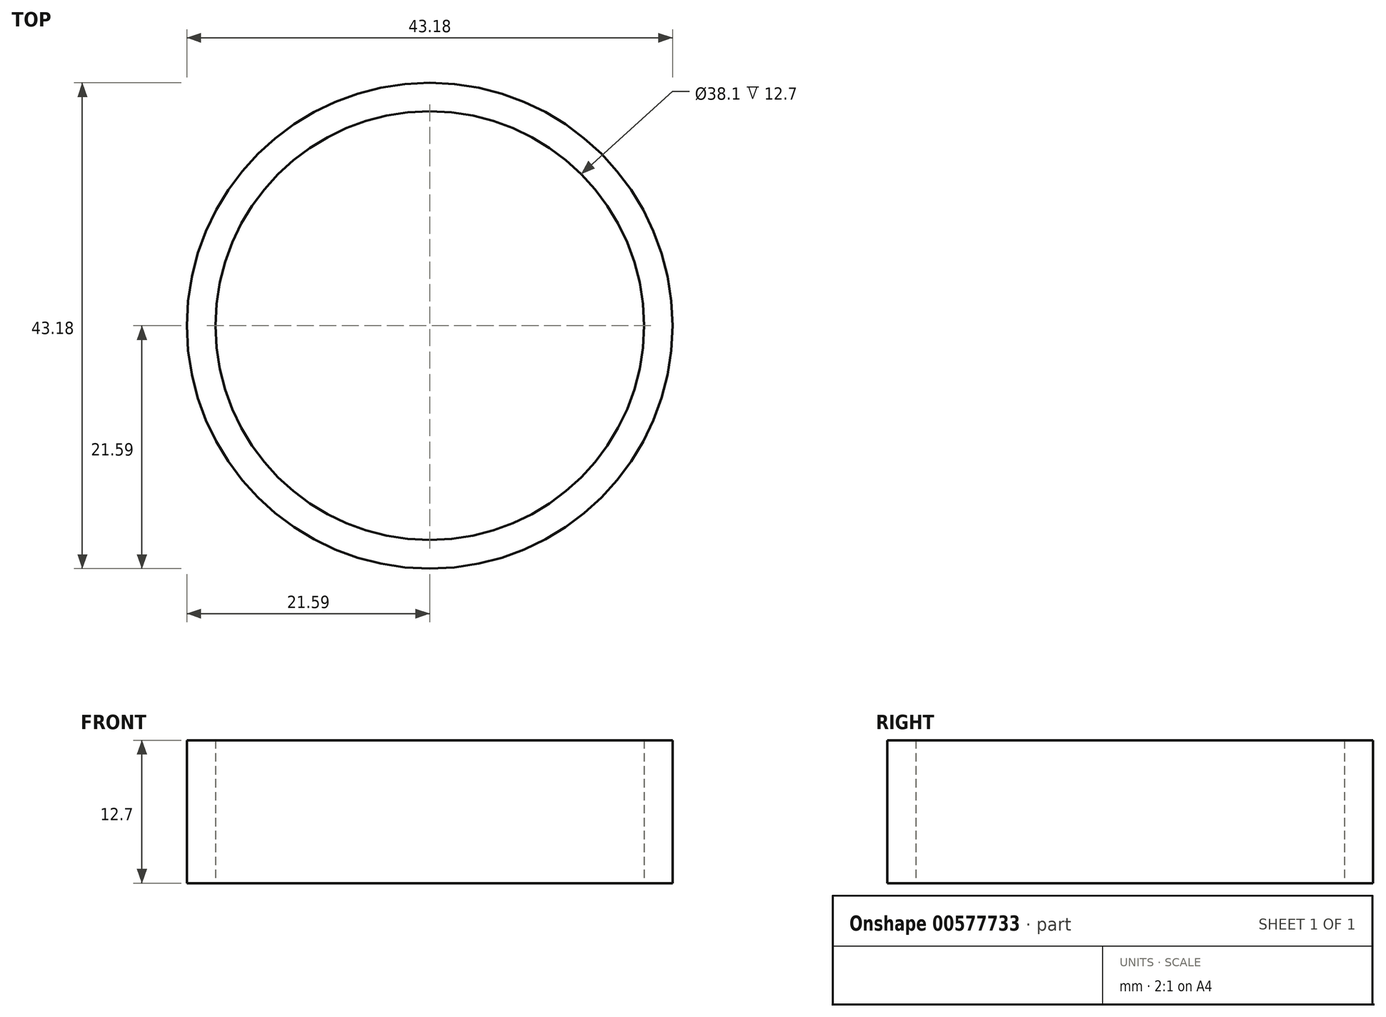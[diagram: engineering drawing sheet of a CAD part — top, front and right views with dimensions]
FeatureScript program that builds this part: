
annotation { "Feature Type Name" : "Feature", "Feature Type Description" : "" }
export const myFeature = defineFeature(function(context is Context, id is Id, definition is map)
    precondition{}
    {
        {
            var Q0;
            Q0=qCreatedBy(makeId("Top.planeOp"),FACE);
            var sketch = newSketch(context, id + "F0", { "sketchPlane" : qUnion([Q0])});
            skCircle(sketch, "E0", {"center": v(0, 0) * mm, "radius": 21.6 * mm});
            skSolve(sketch);
        }
        {
            var Q0;
            Q0=makeQuery(id+"F0.imprint","IMPRINT",FACE,{"disambiguationData":[TD([[makeQuery(id+"F0.imprint","IMPRINT",EDGE,{"derivedFrom":sQuery(id+"F0.wireOp",EDGE,"E0")}),1.0]])]});
            extrude(context, id + "F1", {"entities" : qUnion([Q0]), "depth" : 12.7 * mm, "offsetDistance" : 25.4 * mm});
        }
        {
            var Q0;
            Q0=qCreatedBy(makeId("Top.planeOp"),FACE);
            var sketch = newSketch(context, id + "F2", { "sketchPlane" : qUnion([Q0])});
            skCircle(sketch, "E1", {"center": v(0, 0) * mm, "radius": 19.05 * mm});
            skSolve(sketch);
        }
        {
            var Q0;
            Q0 = qSketchRegion(id + "F2", true);
            extrude(context, id + "F3", {"entities" : qUnion([Q0]), "operationType" : NewBodyOperationType.REMOVE, "depth" : 103.12 * mm, "offsetDistance" : 25.4 * mm});
        }
    });
